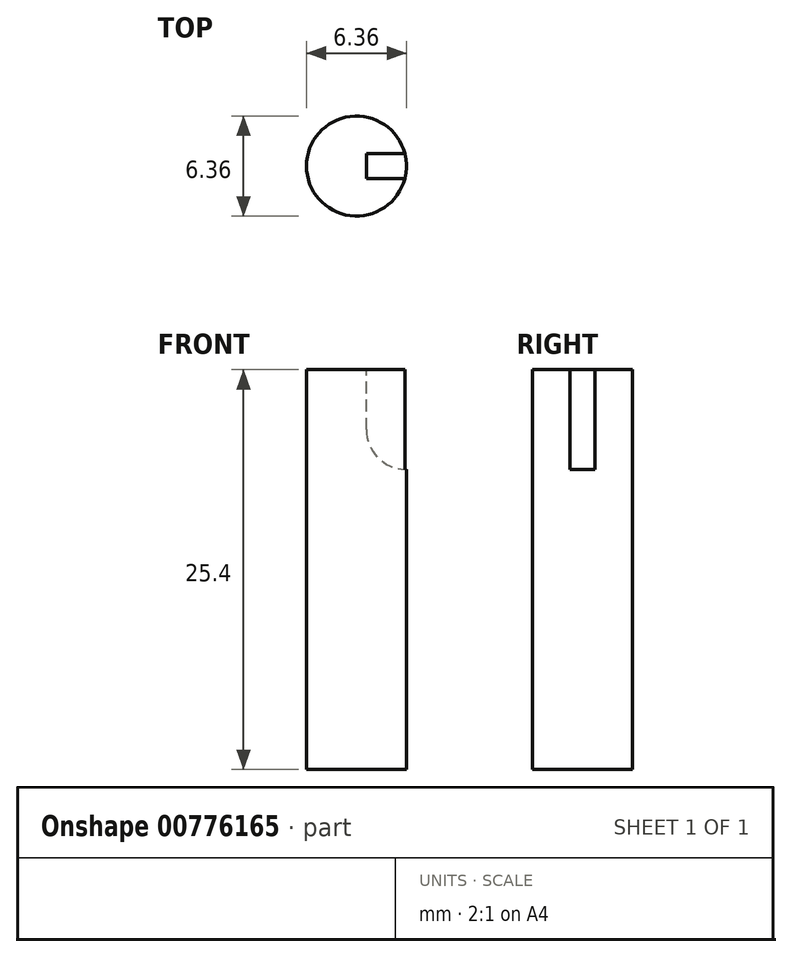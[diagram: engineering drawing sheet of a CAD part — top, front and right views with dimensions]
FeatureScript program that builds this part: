
annotation { "Feature Type Name" : "Feature", "Feature Type Description" : "" }
export const myFeature = defineFeature(function(context is Context, id is Id, definition is map)
    precondition{}
    {
        {
            var Q0;
            Q0=qCreatedBy(makeId("Top.planeOp"),FACE);
            var sketch = newSketch(context, id + "F0", { "sketchPlane" : qUnion([Q0])});
            skCircle(sketch, "E0", {"center": v(0, 0) * mm, "radius": 3.18 * mm});
            skSolve(sketch);
        }
        {
            var Q0;
            Q0 = qSketchRegion(id + "F0", true);
            extrude(context, id + "F1", {"entities" : qUnion([Q0]), "depth" : 25.4 * mm, "offsetDistance" : 25.4 * mm});
        }
        {
            var Q0;
            Q0=makeQuery(id+"F1.opExtrude","CAP_FACE",FACE,{"disambiguationData":[OSD([sQuery(id+"F0.wireOp",EDGE,"E0")])],"isStart":false});
            var sketch = newSketch(context, id + "F2", { "sketchPlane" : qUnion([Q0])});
            skLineSegment(sketch, "E1.bottom", {"start": v(0.63, 0.8) * mm, "end": v(3.18, 0.8) * mm});
            skLineSegment(sketch, "E1.top", {"start": v(0.63, -0.8) * mm, "end": v(3.17, -0.8) * mm});
            skLineSegment(sketch, "E1.left", {"start": v(0.63, 0.8) * mm, "end": v(0.63, -0.8) * mm});
            skLineSegment(sketch, "E1.right", {"start": v(3.18, 0.8) * mm, "end": v(3.18, -0.8) * mm});
            skPoint(sketch, "E1.middle", {"position": v(1.9, 0) * mm});
            skSolve(sketch);
        }
        {
            var Q0;
            Q0 = qSketchRegion(id + "F2", true);
            extrude(context, id + "F3", {"entities" : qUnion([Q0]), "operationType" : NewBodyOperationType.REMOVE, "oppositeDirection" : true, "depth" : 6.35 * mm, "offsetDistance" : 25.4 * mm});
        }
        {
            var Q0;
            Q0=makeQuery(id+"F3.boolean.opBoolean","COPY",EDGE,{"derivedFrom":makeQuery(id+"F3.opExtrude","CAP_EDGE",EDGE,{"disambiguationData":[OSD([sQuery(id+"F2.wireOp",EDGE,"E1.left")])],"isStart":false})});
            fillet(context, id + "F4", {"entities" : qUnion([Q0]), "radius" : 2.54 * mm, "tangentPropagation" : true, "allowEdgeOverflow" : false});
        }
    });
